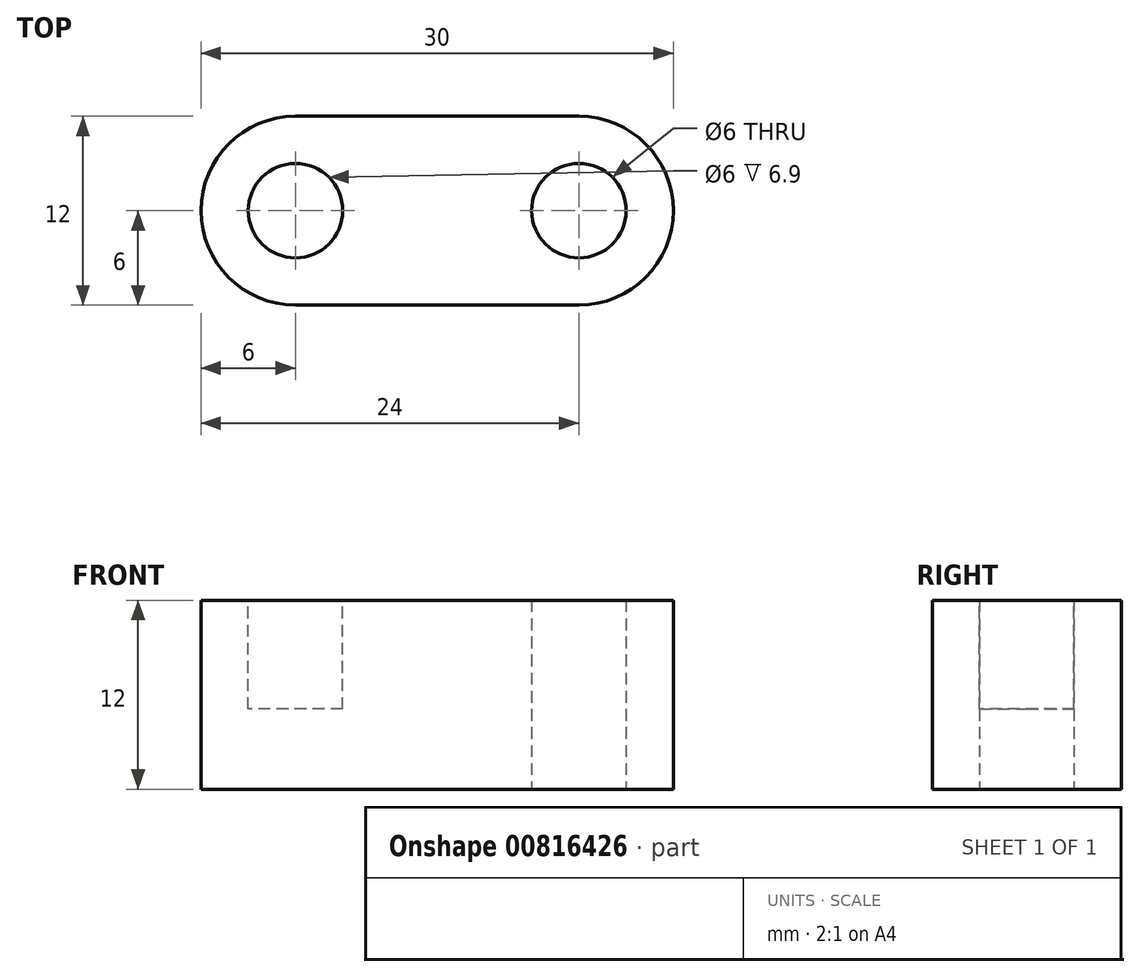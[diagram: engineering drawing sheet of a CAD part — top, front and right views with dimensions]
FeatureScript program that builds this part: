
annotation { "Feature Type Name" : "Feature", "Feature Type Description" : "" }
export const myFeature = defineFeature(function(context is Context, id is Id, definition is map)
    precondition{}
    {
        {
            var Q0;
            Q0=qCreatedBy(makeId("Top.planeOp"),FACE);
            var sketch = newSketch(context, id + "F0", { "sketchPlane" : qUnion([Q0])});
            skLineSegment(sketch, "E0.bottom", {"start": v(-58, 12) * mm, "end": v(-40, 12) * mm});
            skLineSegment(sketch, "E0.top", {"start": v(-58, 0) * mm, "end": v(-40, 0) * mm});
            skLineSegment(sketch, "E0.left", {"start": v(-64, 6) * mm, "end": v(-64, 6) * mm});
            skPoint(sketch, "E1.visualSharp", {"position": v(-64, 12) * mm});
            skArc(sketch, "E1.filletArc", {"start": v(-58, 12) * mm, "mid": v(-62.24, 10.24) * mm, "end": v(-64, 6) * mm});
            skPoint(sketch, "E2.visualSharp", {"position": v(-64, 0) * mm});
            skArc(sketch, "E2.filletArc", {"start": v(-64, 6) * mm, "mid": v(-62.24, 1.76) * mm, "end": v(-58, 0) * mm});
            skArc(sketch, "E3", {"start": v(-40, 0) * mm, "mid": v(-34, 6) * mm, "end": v(-40, 12) * mm});
            skPoint(sketch, "E3.centerSnap0", {"position": v(-35.9, 6) * mm});
            skPoint(sketch, "E4.orphan", {"position": v(-35.9, 12) * mm});
            skPoint(sketch, "E5.orphan", {"position": v(-35.9, 0) * mm});
            skCircle(sketch, "E6", {"center": v(-40, 6) * mm, "radius": 3 * mm});
            skSolve(sketch);
        }
        {
            var Q0;
            Q0 = qSketchRegion(id + "F0", true);
            extrude(context, id + "F1", {"entities" : qUnion([Q0]), "depth" : 12 * mm, "offsetDistance" : 25 * mm});
        }
        {
            var Q0;
            Q0=makeQuery(id+"F1.opExtrude","CAP_FACE",FACE,{"disambiguationData":[OSD([sQuery(id+"F0.wireOp",EDGE,"E0.bottom"),sQuery(id+"F0.wireOp",EDGE,"E0.top"),sQuery(id+"F0.wireOp",EDGE,"E1.filletArc"),sQuery(id+"F0.wireOp",EDGE,"E2.filletArc"),sQuery(id+"F0.wireOp",EDGE,"E3")])],"isStart":false});
            var sketch = newSketch(context, id + "F2", { "sketchPlane" : qUnion([Q0])});
            skCircle(sketch, "E7", {"center": v(-58, 6) * mm, "radius": 3 * mm});
            skSolve(sketch);
        }
        {
            var Q0;
            Q0 = qSketchRegion(id + "F2", true);
            extrude(context, id + "F3", {"entities" : qUnion([Q0]), "operationType" : NewBodyOperationType.REMOVE, "oppositeDirection" : true, "depth" : 6.9 * mm, "offsetDistance" : 25 * mm});
        }
    });
